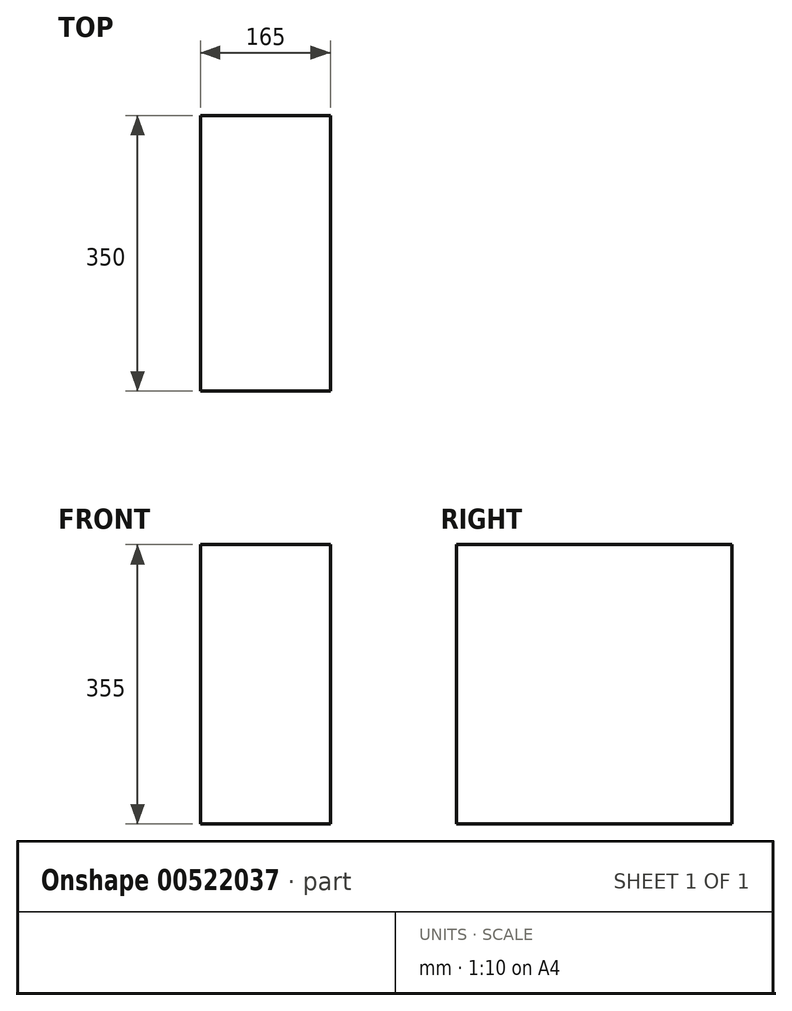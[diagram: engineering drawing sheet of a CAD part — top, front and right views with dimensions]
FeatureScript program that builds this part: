
annotation { "Feature Type Name" : "Feature", "Feature Type Description" : "" }
export const myFeature = defineFeature(function(context is Context, id is Id, definition is map)
    precondition{}
    {
        {
            var Q0;
            Q0=qCreatedBy(makeId("Top.planeOp"),FACE);
            var sketch = newSketch(context, id + "F0", { "sketchPlane" : qUnion([Q0])});
            skLineSegment(sketch, "E0.bottom", {"start": v(0, 0) * mm, "end": v(165, 0) * mm});
            skLineSegment(sketch, "E0.top", {"start": v(0, 350) * mm, "end": v(165, 350) * mm});
            skLineSegment(sketch, "E0.left", {"start": v(0, 0) * mm, "end": v(0, 350) * mm});
            skLineSegment(sketch, "E0.right", {"start": v(165, 0) * mm, "end": v(165, 350) * mm});
            skSolve(sketch);
        }
        {
            var Q0;
            Q0=makeQuery(id+"F0.imprint","IMPRINT",FACE,{"disambiguationData":[TD([[makeQuery(id+"F0.imprint","IMPRINT",EDGE,{"derivedFrom":sQuery(id+"F0.wireOp",EDGE,"E0.bottom")}),1.0]])]});
            extrude(context, id + "F1", {"entities" : qUnion([Q0]), "depth" : 355 * mm, "offsetDistance" : 25 * mm});
        }
    });
